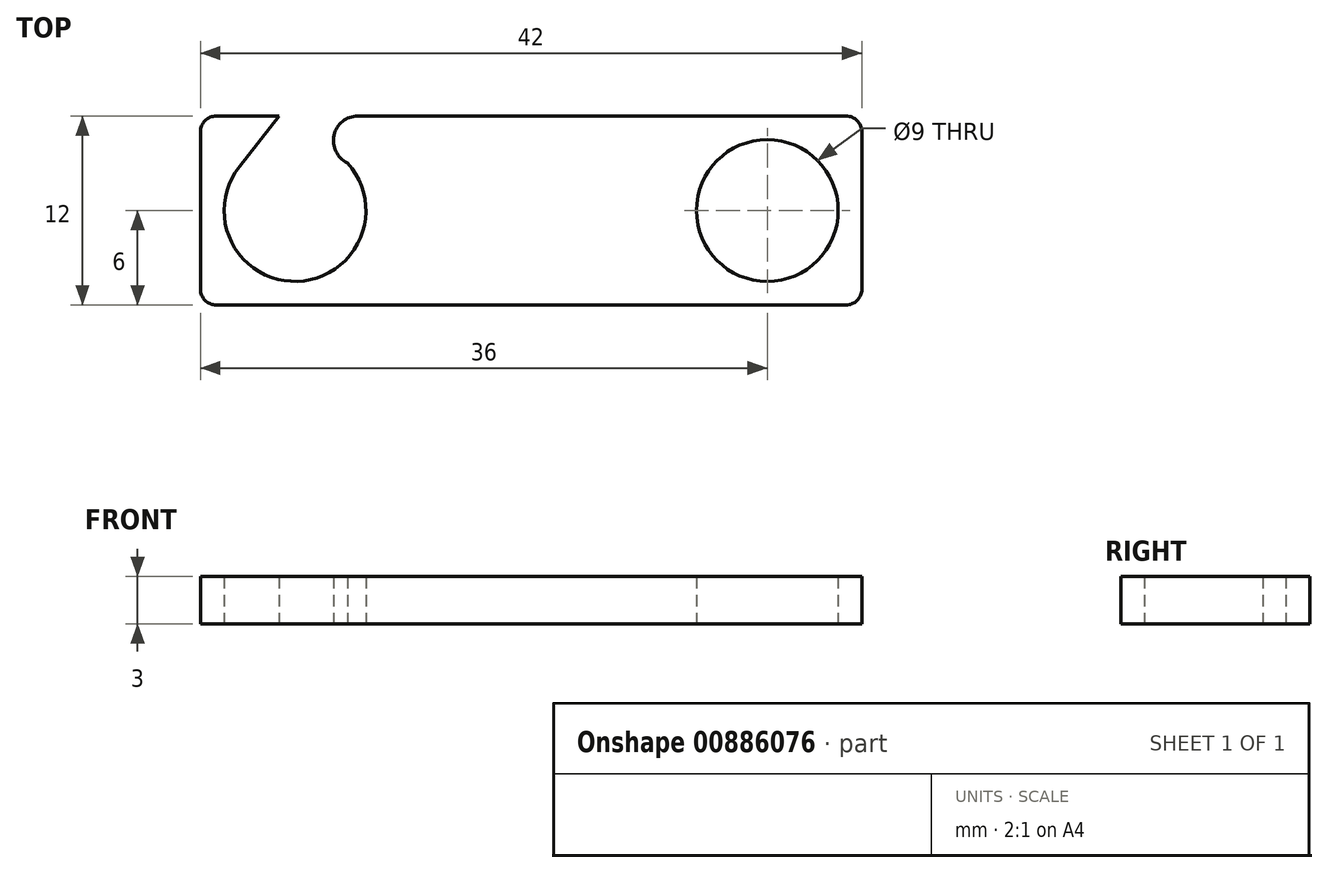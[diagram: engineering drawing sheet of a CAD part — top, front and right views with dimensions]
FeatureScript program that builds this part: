
annotation { "Feature Type Name" : "Feature", "Feature Type Description" : "" }
export const myFeature = defineFeature(function(context is Context, id is Id, definition is map)
    precondition{}
    {
        {
            var Q0;
            Q0=qCreatedBy(makeId("Top.planeOp"),FACE);
            var sketch = newSketch(context, id + "F0", { "sketchPlane" : qUnion([Q0])});
            skLineSegment(sketch, "E0", {"start": v(-20, 6) * mm, "end": v(-16, 6) * mm});
            skLineSegment(sketch, "E1", {"start": v(-20, -6) * mm, "end": v(20, -6) * mm});
            skLineSegment(sketch, "E2", {"start": v(21, 5) * mm, "end": v(21, -5) * mm});
            skLineSegment(sketch, "E3", {"start": v(-21, 5) * mm, "end": v(-21, -5) * mm});
            skArc(sketch, "E4", {"start": v(-21, 5) * mm, "mid": v(-20.7, 5.7) * mm, "end": v(-20, 6) * mm});
            skArc(sketch, "E5", {"start": v(20, 6) * mm, "mid": v(20.7, 5.7) * mm, "end": v(21, 5) * mm});
            skArc(sketch, "E6", {"start": v(21, -5) * mm, "mid": v(20.7, -5.7) * mm, "end": v(20, -6) * mm});
            skArc(sketch, "E7", {"start": v(-20, -6) * mm, "mid": v(-20.7, -5.7) * mm, "end": v(-21, -5) * mm});
            skCircle(sketch, "E8", {"center": v(15, 0) * mm, "radius": 4.5 * mm});
            skArc(sketch, "E9", {"start": v(-18.53, 2.79) * mm, "mid": v(-14.84, -4.5) * mm, "end": v(-11.67, 3.02) * mm});
            skLineSegment(sketch, "E10", {"start": v(-16, 6) * mm, "end": v(-18.53, 2.79) * mm});
            skLineSegment(sketch, "E11.trimOffspring", {"start": v(-11, 6) * mm, "end": v(20, 6) * mm});
            skArc(sketch, "E12", {"start": v(-11, 6) * mm, "mid": v(-12.53, 4.78) * mm, "end": v(-11.67, 3.02) * mm});
            skSolve(sketch);
        }
        {
            var Q0;
            Q0=makeQuery(id+"F0.imprint","IMPRINT",FACE,{"disambiguationData":[TD([[makeQuery(id+"F0.imprint","IMPRINT",EDGE,{"derivedFrom":sQuery(id+"F0.wireOp",EDGE,"E0")}),-1.0]])]});
            extrude(context, id + "F1", {"entities" : qUnion([Q0]), "depth" : 3 * mm, "offsetDistance" : 25 * mm});
        }
    });
